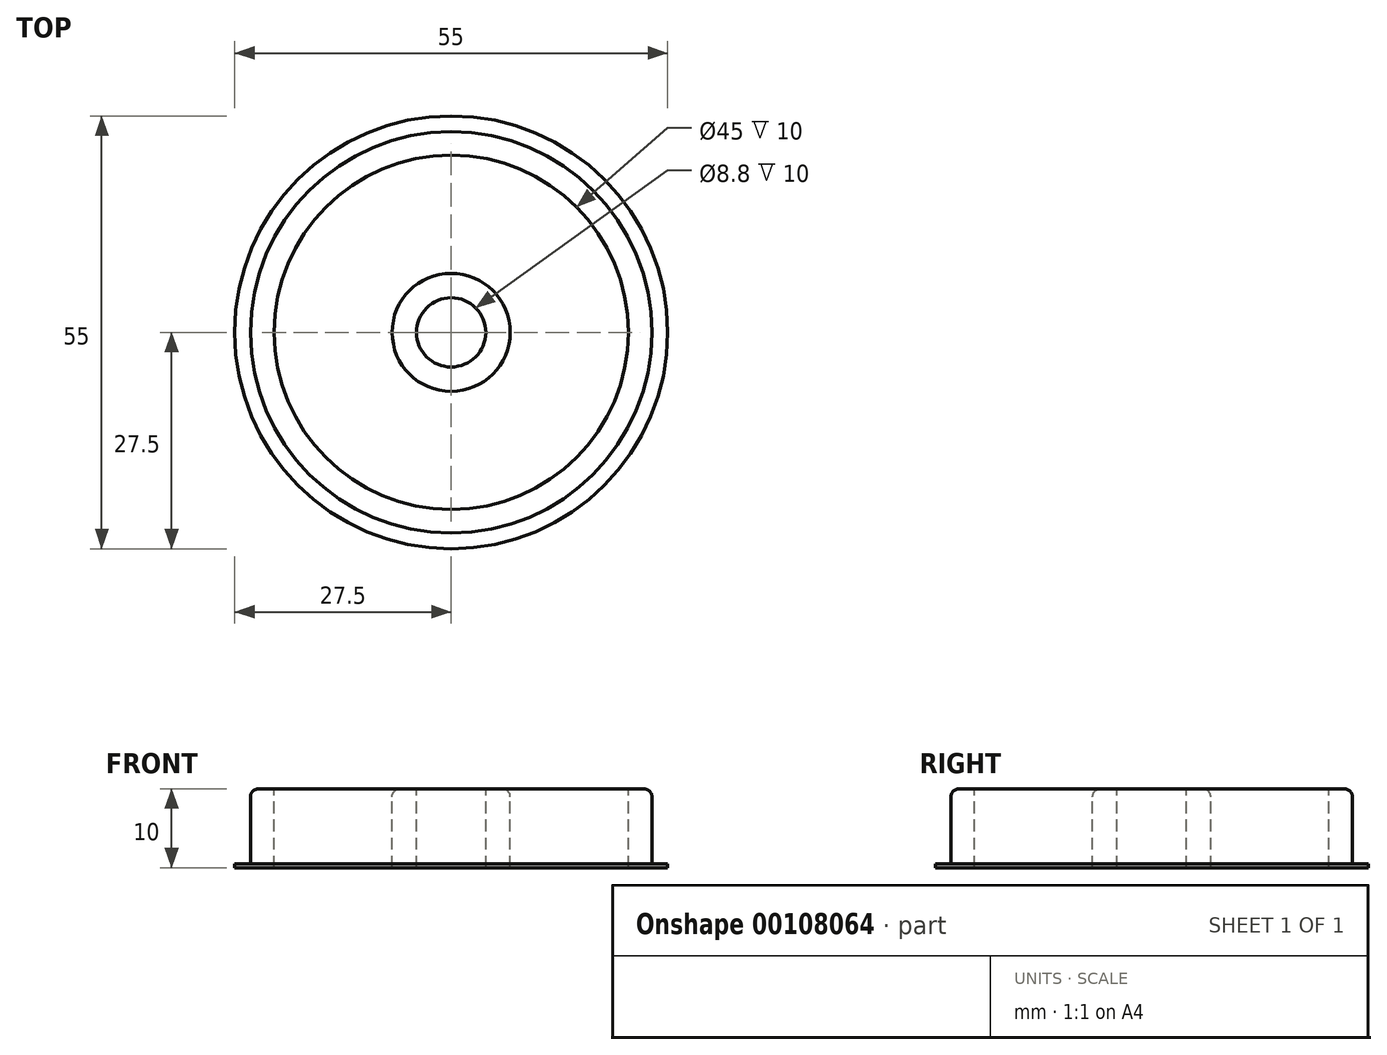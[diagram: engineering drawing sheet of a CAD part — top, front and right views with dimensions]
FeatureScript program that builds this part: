
annotation { "Feature Type Name" : "Feature", "Feature Type Description" : "" }
export const myFeature = defineFeature(function(context is Context, id is Id, definition is map)
    precondition{}
    {
        {
            var Q0;
            Q0=qCreatedBy(makeId("Top.planeOp"),FACE);
            var sketch = newSketch(context, id + "F0", { "sketchPlane" : qUnion([Q0])});
            skCircle(sketch, "E0", {"center": v(0, 0) * mm, "radius": 25.5 * mm});
            skCircle(sketch, "E1", {"center": v(0, 0) * mm, "radius": 27.5 * mm});
            skSolve(sketch);
        }
        {
            var Q0;
            Q0=makeQuery(id+"F0.imprint","IMPRINT",FACE,{"disambiguationData":[TD([[makeQuery(id+"F0.imprint","IMPRINT",EDGE,{"derivedFrom":sQuery(id+"F0.wireOp",EDGE,"E0")}),1.0]])]});
            extrude(context, id + "F1", {"entities" : qUnion([Q0]), "depth" : 10 * mm});
        }
        {
            var Q0;
            Q0=makeQuery(id+"F0.imprint","IMPRINT",FACE,{"disambiguationData":[TD([[makeQuery(id+"F0.imprint","IMPRINT",EDGE,{"derivedFrom":sQuery(id+"F0.wireOp",EDGE,"E0")}),-1.0]])]});
            extrude(context, id + "F2", {"entities" : qUnion([Q0]), "operationType" : NewBodyOperationType.ADD, "depth" : 0.5 * mm});
        }
        {
            var Q0;
            Q0=makeQuery(id+"F1.opExtrude","CAP_FACE",FACE,{"disambiguationData":[OSD([sQuery(id+"F0.wireOp",EDGE,"E0")])],"isStart":false});
            var sketch = newSketch(context, id + "F3", { "sketchPlane" : qUnion([Q0])});
            skCircle(sketch, "E2", {"center": v(0, 0) * mm, "radius": 22.5 * mm});
            skCircle(sketch, "E3", {"center": v(0, 0) * mm, "radius": 7.5 * mm});
            skSolve(sketch);
        }
        {
            var Q0;
            Q0=makeQuery(id+"F3.imprint","IMPRINT",FACE,{"disambiguationData":[TD([[makeQuery(id+"F3.imprint","IMPRINT",EDGE,{"derivedFrom":sQuery(id+"F3.wireOp",EDGE,"E2")}),1.0]])]});
            extrude(context, id + "F4", {"entities" : qUnion([Q0]), "operationType" : NewBodyOperationType.REMOVE, "endBound" : BoundingType.THROUGH_ALL, "oppositeDirection" : true, "depth" : 25 * mm});
        }
        {
            var Q0;
            Q0=makeQuery(id+"F1.opExtrude","CAP_FACE",FACE,{"disambiguationData":[OSD([sQuery(id+"F0.wireOp",EDGE,"E0")])],"isStart":false});
            var sketch = newSketch(context, id + "F5", { "sketchPlane" : qUnion([Q0])});
            skCircle(sketch, "E4", {"center": v(0, 0) * mm, "radius": 7.5 * mm, "construction": true});
            skCircle(sketch, "E5", {"center": v(0, 0) * mm, "radius": 22.5 * mm, "construction": true});
            skLineSegment(sketch, "E6", {"start": v(22.5, -2.5) * mm, "end": v(22.5, 2.5) * mm});
            skPoint(sketch, "E7", {"position": v(22.5, 0) * mm});
            skLineSegment(sketch, "E8", {"start": v(6.9, 2.5) * mm, "end": v(6.9, -2.5) * mm});
            skPoint(sketch, "E9", {"position": v(6.9, 0) * mm});
            skLineSegment(sketch, "E10", {"start": v(6.9, 2.5) * mm, "end": v(22.5, 2.5) * mm});
            skLineSegment(sketch, "E11", {"start": v(22.5, -2.5) * mm, "end": v(6.9, -2.5) * mm});
            skSolve(sketch);
        }
        {
            var Q0;
            {var subQ4=sQuery(id+"F5.wireOp",EDGE,"E10");var subQ5=makeQuery(id+"F4.boolean.opBoolean","COPY",EDGE,{"derivedFrom":makeQuery(id+"F4.opExtrude","CAP_EDGE",EDGE,{"disambiguationData":[OSD([sQuery(id+"F3.wireOp",EDGE,"E3")])],"isStart":true})});var subQ6=makeQuery(id+"F5.imprint","INTERSECT",VERTEX,{"derivedFrom":[subQ5,subQ4]});Q0=makeQuery(id+"F5.imprint","IMPRINT",FACE,{"disambiguationData":[TD([[makeQuery(id+"F5.imprint","IMPRINT",EDGE,{"disambiguationData":[TD([[subQ6,-1.0]])],"derivedFrom":subQ4}),-1.0]])]});}
            var Q1;
            {var subQ0=sQuery(id+"F0.wireOp",EDGE,"E0");Q1=makeQuery(id+"F4.boolean.opBoolean","SPLIT",FACE,{"disambiguationData":[TD([makeQuery(id+"F4.opExtrude","SWEPT_FACE",FACE,{"disambiguationData":[OSD([sQuery(id+"F3.wireOp",EDGE,"E3")])]})])],"derivedFrom":makeQuery(id+"F2.boolean.opBoolean","MERGE",FACE,{"derivedFrom":[makeQuery(id+"F1.opExtrude","CAP_FACE",FACE,{"disambiguationData":[OSD([subQ0])],"isStart":true}),makeQuery(id+"F2.opExtrude","CAP_FACE",FACE,{"disambiguationData":[OSD([subQ0,sQuery(id+"F0.wireOp",EDGE,"E1")])],"isStart":true})]})});}
            extrude(context, id + "F6", {"entities" : qUnion([Q0]), "operationType" : NewBodyOperationType.ADD, "endBound" : BoundingType.UP_TO_SURFACE, "oppositeDirection" : true, "endBoundEntityFace" : qUnion([Q1]), "depth" : 25 * mm});
        }
        {
            var Q0;
            {var subQ0=sQuery(id+"F5.wireOp",EDGE,"E11");var subQ1=sQuery(id+"F5.wireOp",EDGE,"E10");var subQ3=sQuery(id+"F3.wireOp",EDGE,"E2");var subQ5=makeQuery(id+"F5tnbVkuxQUPv66_1.1.F6.opExtrude","SWEPT_FACE",FACE,{"disambiguationData":[OSD([subQ1])]});Q0=makeQuery(id+"F5tnbVkuxQUPv66_1.2.F6.boolean.opBoolean","SPLIT",EDGE,{"disambiguationData":[TD([subQ5])],"derivedFrom":makeQuery(id+"F5tnbVkuxQUPv66_1.1.F6.boolean.opBoolean","SPLIT",EDGE,{"disambiguationData":[TD([makeQuery(id+"F6.opExtrude","SWEPT_FACE",FACE,{"disambiguationData":[OSD([subQ0])]})])],"derivedFrom":makeQuery(id+"F4.boolean.opBoolean","COPY",EDGE,{"derivedFrom":makeQuery(id+"F4.opExtrude","CAP_EDGE",EDGE,{"disambiguationData":[OSD([subQ3])],"isStart":true})})})});}
            var Q1;
            Q1=makeQuery(id+"F5tnbVkuxQUPv66_1.1.F6.opExtrude","CAP_EDGE",EDGE,{"disambiguationData":[OSD([sQuery(id+"F5.wireOp",EDGE,"E10")])],"isStart":true});
            var Q2;
            Q2=makeQuery(id+"F5tnbVkuxQUPv66_1.1.F6.opExtrude","CAP_EDGE",EDGE,{"disambiguationData":[OSD([sQuery(id+"F5.wireOp",EDGE,"E11")])],"isStart":true});
            var Q3;
            {var subQ1=sQuery(id+"F5.wireOp",EDGE,"E10");var subQ3=sQuery(id+"F3.wireOp",EDGE,"E2");Q3=makeQuery(id+"F5tnbVkuxQUPv66_1.1.F6.boolean.opBoolean","SPLIT",EDGE,{"disambiguationData":[TD([makeQuery(id+"F6.opExtrude","SWEPT_FACE",FACE,{"disambiguationData":[OSD([subQ1])]})])],"derivedFrom":makeQuery(id+"F4.boolean.opBoolean","COPY",EDGE,{"derivedFrom":makeQuery(id+"F4.opExtrude","CAP_EDGE",EDGE,{"disambiguationData":[OSD([subQ3])],"isStart":true})})});}
            var Q4;
            Q4=makeQuery(id+"F6.opExtrude","CAP_EDGE",EDGE,{"disambiguationData":[OSD([sQuery(id+"F5.wireOp",EDGE,"E10")])],"isStart":true});
            var Q5;
            {var subQ1=sQuery(id+"F5.wireOp",EDGE,"E10");var subQ2=sQuery(id+"F3.wireOp",EDGE,"E3");Q5=makeQuery(id+"F5tnbVkuxQUPv66_1.1.F6.boolean.opBoolean","SPLIT",EDGE,{"disambiguationData":[TD([makeQuery(id+"F6.opExtrude","SWEPT_FACE",FACE,{"disambiguationData":[OSD([subQ1])]})])],"derivedFrom":makeQuery(id+"F4.boolean.opBoolean","COPY",EDGE,{"derivedFrom":makeQuery(id+"F4.opExtrude","CAP_EDGE",EDGE,{"disambiguationData":[OSD([subQ2])],"isStart":true})})});}
            var Q6;
            {var subQ0=sQuery(id+"F5.wireOp",EDGE,"E10");var subQ1=makeQuery(id+"F5tnbVkuxQUPv66_1.1.F6.opExtrude","SWEPT_FACE",FACE,{"disambiguationData":[OSD([subQ0])]});var subQ2=sQuery(id+"F5.wireOp",EDGE,"E11");var subQ3=sQuery(id+"F3.wireOp",EDGE,"E3");Q6=makeQuery(id+"F5tnbVkuxQUPv66_1.2.F6.boolean.opBoolean","SPLIT",EDGE,{"disambiguationData":[TD([subQ1])],"derivedFrom":makeQuery(id+"F5tnbVkuxQUPv66_1.1.F6.boolean.opBoolean","SPLIT",EDGE,{"disambiguationData":[TD([makeQuery(id+"F6.opExtrude","SWEPT_FACE",FACE,{"disambiguationData":[OSD([subQ2])]})])],"derivedFrom":makeQuery(id+"F4.boolean.opBoolean","COPY",EDGE,{"derivedFrom":makeQuery(id+"F4.opExtrude","CAP_EDGE",EDGE,{"disambiguationData":[OSD([subQ3])],"isStart":true})})})});}
            var Q7;
            Q7=makeQuery(id+"F5tnbVkuxQUPv66_1.2.F6.opExtrude","CAP_EDGE",EDGE,{"disambiguationData":[OSD([sQuery(id+"F5.wireOp",EDGE,"E11")])],"isStart":true});
            var Q8;
            Q8=makeQuery(id+"F5tnbVkuxQUPv66_1.2.F6.opExtrude","CAP_EDGE",EDGE,{"disambiguationData":[OSD([sQuery(id+"F5.wireOp",EDGE,"E10")])],"isStart":true});
            var Q9;
            {var subQ0=sQuery(id+"F5.wireOp",EDGE,"E11");var subQ1=sQuery(id+"F5.wireOp",EDGE,"E10");var subQ2=sQuery(id+"F3.wireOp",EDGE,"E3");var subQ8=makeQuery(id+"F5tnbVkuxQUPv66_1.2.F6.opExtrude","SWEPT_FACE",FACE,{"disambiguationData":[OSD([subQ1])]});var subQ10=makeQuery(id+"F6.opExtrude","SWEPT_FACE",FACE,{"disambiguationData":[OSD([subQ0])]});Q9=makeQuery(id+"F5tnbVkuxQUPv66_1.3.F6.boolean.opBoolean","SPLIT",EDGE,{"disambiguationData":[TD([subQ8])],"derivedFrom":makeQuery(id+"F5tnbVkuxQUPv66_1.2.F6.boolean.opBoolean","SPLIT",EDGE,{"disambiguationData":[TD([subQ10])],"derivedFrom":makeQuery(id+"F5tnbVkuxQUPv66_1.1.F6.boolean.opBoolean","SPLIT",EDGE,{"disambiguationData":[TD([subQ10])],"derivedFrom":makeQuery(id+"F4.boolean.opBoolean","COPY",EDGE,{"derivedFrom":makeQuery(id+"F4.opExtrude","CAP_EDGE",EDGE,{"disambiguationData":[OSD([subQ2])],"isStart":true})})})})});}
            var Q10;
            {var subQ0=sQuery(id+"F5.wireOp",EDGE,"E11");var subQ2=sQuery(id+"F3.wireOp",EDGE,"E3");var subQ5=makeQuery(id+"F6.opExtrude","SWEPT_FACE",FACE,{"disambiguationData":[OSD([subQ0])]});Q10=makeQuery(id+"F5tnbVkuxQUPv66_1.3.F6.boolean.opBoolean","SPLIT",EDGE,{"disambiguationData":[TD([subQ5])],"derivedFrom":makeQuery(id+"F5tnbVkuxQUPv66_1.2.F6.boolean.opBoolean","SPLIT",EDGE,{"disambiguationData":[TD([subQ5])],"derivedFrom":makeQuery(id+"F5tnbVkuxQUPv66_1.1.F6.boolean.opBoolean","SPLIT",EDGE,{"disambiguationData":[TD([subQ5])],"derivedFrom":makeQuery(id+"F4.boolean.opBoolean","COPY",EDGE,{"derivedFrom":makeQuery(id+"F4.opExtrude","CAP_EDGE",EDGE,{"disambiguationData":[OSD([subQ2])],"isStart":true})})})})});}
            var Q11;
            Q11=makeQuery(id+"F6.opExtrude","CAP_EDGE",EDGE,{"disambiguationData":[OSD([sQuery(id+"F5.wireOp",EDGE,"E11")])],"isStart":true});
            var Q12;
            Q12=makeQuery(id+"F5tnbVkuxQUPv66_1.3.F6.opExtrude","CAP_EDGE",EDGE,{"disambiguationData":[OSD([sQuery(id+"F5.wireOp",EDGE,"E10")])],"isStart":true});
            var Q13;
            Q13=makeQuery(id+"F5tnbVkuxQUPv66_1.3.F6.opExtrude","CAP_EDGE",EDGE,{"disambiguationData":[OSD([sQuery(id+"F5.wireOp",EDGE,"E11")])],"isStart":true});
            var Q14;
            {var subQ0=sQuery(id+"F5.wireOp",EDGE,"E11");var subQ1=sQuery(id+"F5.wireOp",EDGE,"E10");var subQ3=sQuery(id+"F3.wireOp",EDGE,"E2");var subQ8=makeQuery(id+"F5tnbVkuxQUPv66_1.2.F6.opExtrude","SWEPT_FACE",FACE,{"disambiguationData":[OSD([subQ1])]});var subQ10=makeQuery(id+"F6.opExtrude","SWEPT_FACE",FACE,{"disambiguationData":[OSD([subQ0])]});Q14=makeQuery(id+"F5tnbVkuxQUPv66_1.3.F6.boolean.opBoolean","SPLIT",EDGE,{"disambiguationData":[TD([subQ8])],"derivedFrom":makeQuery(id+"F5tnbVkuxQUPv66_1.2.F6.boolean.opBoolean","SPLIT",EDGE,{"disambiguationData":[TD([subQ10])],"derivedFrom":makeQuery(id+"F5tnbVkuxQUPv66_1.1.F6.boolean.opBoolean","SPLIT",EDGE,{"disambiguationData":[TD([subQ10])],"derivedFrom":makeQuery(id+"F4.boolean.opBoolean","COPY",EDGE,{"derivedFrom":makeQuery(id+"F4.opExtrude","CAP_EDGE",EDGE,{"disambiguationData":[OSD([subQ3])],"isStart":true})})})})});}
            var Q15;
            {var subQ0=sQuery(id+"F5.wireOp",EDGE,"E11");var subQ3=sQuery(id+"F3.wireOp",EDGE,"E2");var subQ7=makeQuery(id+"F6.opExtrude","SWEPT_FACE",FACE,{"disambiguationData":[OSD([subQ0])]});Q15=makeQuery(id+"F5tnbVkuxQUPv66_1.3.F6.boolean.opBoolean","SPLIT",EDGE,{"disambiguationData":[TD([subQ7])],"derivedFrom":makeQuery(id+"F5tnbVkuxQUPv66_1.2.F6.boolean.opBoolean","SPLIT",EDGE,{"disambiguationData":[TD([subQ7])],"derivedFrom":makeQuery(id+"F5tnbVkuxQUPv66_1.1.F6.boolean.opBoolean","SPLIT",EDGE,{"disambiguationData":[TD([subQ7])],"derivedFrom":makeQuery(id+"F4.boolean.opBoolean","COPY",EDGE,{"derivedFrom":makeQuery(id+"F4.opExtrude","CAP_EDGE",EDGE,{"disambiguationData":[OSD([subQ3])],"isStart":true})})})})});}
            var Q16;
            Q16=makeQuery(id+"F1.opExtrude","CAP_EDGE",EDGE,{"disambiguationData":[OSD([sQuery(id+"F0.wireOp",EDGE,"E0")])],"isStart":false});
            var Q17;
            Q17=makeQuery(id+"F5tnbVkuxQUPv66_1.1.F6.opExtrude","SWEPT_EDGE",EDGE,{"disambiguationData":[OSD([sQuery(id+"F3.wireOp",EDGE,"E2"),sQuery(id+"F5.wireOp",EDGE,"E10")])]});
            var Q18;
            Q18=makeQuery(id+"F5tnbVkuxQUPv66_1.1.F6.opExtrude","SWEPT_EDGE",EDGE,{"disambiguationData":[OSD([sQuery(id+"F3.wireOp",EDGE,"E2"),sQuery(id+"F5.wireOp",EDGE,"E11")])]});
            var Q19;
            Q19=makeQuery(id+"F6.opExtrude","SWEPT_EDGE",EDGE,{"disambiguationData":[OSD([sQuery(id+"F3.wireOp",EDGE,"E2"),sQuery(id+"F5.wireOp",EDGE,"E10")])]});
            var Q20;
            Q20=makeQuery(id+"F6.opExtrude","SWEPT_EDGE",EDGE,{"disambiguationData":[OSD([sQuery(id+"F3.wireOp",EDGE,"E3"),sQuery(id+"F5.wireOp",EDGE,"E10")])]});
            var Q21;
            Q21=makeQuery(id+"F5tnbVkuxQUPv66_1.1.F6.opExtrude","SWEPT_EDGE",EDGE,{"disambiguationData":[OSD([sQuery(id+"F3.wireOp",EDGE,"E3"),sQuery(id+"F5.wireOp",EDGE,"E11")])]});
            var Q22;
            Q22=makeQuery(id+"F5tnbVkuxQUPv66_1.1.F6.opExtrude","SWEPT_EDGE",EDGE,{"disambiguationData":[OSD([sQuery(id+"F3.wireOp",EDGE,"E3"),sQuery(id+"F5.wireOp",EDGE,"E10")])]});
            var Q23;
            Q23=makeQuery(id+"F5tnbVkuxQUPv66_1.2.F6.opExtrude","SWEPT_EDGE",EDGE,{"disambiguationData":[OSD([sQuery(id+"F3.wireOp",EDGE,"E3"),sQuery(id+"F5.wireOp",EDGE,"E11")])]});
            var Q24;
            Q24=makeQuery(id+"F5tnbVkuxQUPv66_1.2.F6.opExtrude","SWEPT_EDGE",EDGE,{"disambiguationData":[OSD([sQuery(id+"F3.wireOp",EDGE,"E2"),sQuery(id+"F5.wireOp",EDGE,"E11")])]});
            var Q25;
            Q25=makeQuery(id+"F5tnbVkuxQUPv66_1.2.F6.opExtrude","SWEPT_EDGE",EDGE,{"disambiguationData":[OSD([sQuery(id+"F3.wireOp",EDGE,"E2"),sQuery(id+"F5.wireOp",EDGE,"E10")])]});
            var Q26;
            Q26=makeQuery(id+"F5tnbVkuxQUPv66_1.2.F6.opExtrude","SWEPT_EDGE",EDGE,{"disambiguationData":[OSD([sQuery(id+"F3.wireOp",EDGE,"E3"),sQuery(id+"F5.wireOp",EDGE,"E10")])]});
            var Q27;
            Q27=makeQuery(id+"F5tnbVkuxQUPv66_1.3.F6.opExtrude","SWEPT_EDGE",EDGE,{"disambiguationData":[OSD([sQuery(id+"F3.wireOp",EDGE,"E3"),sQuery(id+"F5.wireOp",EDGE,"E11")])]});
            var Q28;
            Q28=makeQuery(id+"F5tnbVkuxQUPv66_1.3.F6.opExtrude","SWEPT_EDGE",EDGE,{"disambiguationData":[OSD([sQuery(id+"F3.wireOp",EDGE,"E2"),sQuery(id+"F5.wireOp",EDGE,"E11")])]});
            var Q29;
            Q29=makeQuery(id+"F6.opExtrude","SWEPT_EDGE",EDGE,{"disambiguationData":[OSD([sQuery(id+"F3.wireOp",EDGE,"E3"),sQuery(id+"F5.wireOp",EDGE,"E11")])]});
            var Q30;
            Q30=makeQuery(id+"F5tnbVkuxQUPv66_1.3.F6.opExtrude","SWEPT_EDGE",EDGE,{"disambiguationData":[OSD([sQuery(id+"F3.wireOp",EDGE,"E3"),sQuery(id+"F5.wireOp",EDGE,"E10")])]});
            var Q31;
            Q31=makeQuery(id+"F5tnbVkuxQUPv66_1.3.F6.opExtrude","SWEPT_EDGE",EDGE,{"disambiguationData":[OSD([sQuery(id+"F3.wireOp",EDGE,"E2"),sQuery(id+"F5.wireOp",EDGE,"E10")])]});
            var Q32;
            Q32=makeQuery(id+"F6.opExtrude","SWEPT_EDGE",EDGE,{"disambiguationData":[OSD([sQuery(id+"F3.wireOp",EDGE,"E2"),sQuery(id+"F5.wireOp",EDGE,"E11")])]});
            fillet(context, id + "F7", {"entities" : qUnion([Q0, Q1, Q2, Q3, Q4, Q5, Q6, Q7, Q8, Q9, Q10, Q11, Q12, Q13, Q14, Q15, Q16, Q17, Q18, Q19, Q20, Q21, Q22, Q23, Q24, Q25, Q26, Q27, Q28, Q29, Q30, Q31, Q32]), "radius" : 1 * mm, "tangentPropagation" : true, "allowEdgeOverflow" : false});
        }
        {
            var Q0;
            {var subQ0=sQuery(id+"F5.wireOp",EDGE,"E11");var subQ1=sQuery(id+"F5.wireOp",EDGE,"E10");var subQ2=sQuery(id+"F3.wireOp",EDGE,"E3");var subQ3=sQuery(id+"F3.wireOp",EDGE,"E2");var subQ4=sQuery(id+"F0.wireOp",EDGE,"E0");var subQ5=makeQuery(id+"F1.opExtrude","CAP_FACE",FACE,{"disambiguationData":[OSD([subQ4])],"isStart":false});Q0=makeQuery(id+"F5tnbVkuxQUPv66_1.3.F6.boolean.opBoolean","MERGE",FACE,{"derivedFrom":[makeQuery(id+"F5tnbVkuxQUPv66_1.2.F6.boolean.opBoolean","MERGE",FACE,{"derivedFrom":[makeQuery(id+"F5tnbVkuxQUPv66_1.1.F6.boolean.opBoolean","MERGE",FACE,{"derivedFrom":[makeQuery(id+"F6.boolean.opBoolean","MERGE",FACE,{"derivedFrom":[makeQuery(id+"F4.boolean.opBoolean","SPLIT",FACE,{"disambiguationData":[TD([makeQuery(id+"F1.opExtrude","SWEPT_FACE",FACE,{"disambiguationData":[OSD([subQ4])]})])],"derivedFrom":subQ5}),makeQuery(id+"F4.boolean.opBoolean","SPLIT",FACE,{"disambiguationData":[TD([makeQuery(id+"F4.opExtrude","SWEPT_FACE",FACE,{"disambiguationData":[OSD([subQ2])]})])],"derivedFrom":subQ5}),makeQuery(id+"F6.opExtrude","CAP_FACE",FACE,{"disambiguationData":[OSD([subQ3,subQ2,subQ1,subQ0])],"isStart":true})]}),makeQuery(id+"F5tnbVkuxQUPv66_1.1.F6.opExtrude","CAP_FACE",FACE,{"disambiguationData":[OSD([subQ3,subQ2,subQ1,subQ0])],"isStart":true})]}),makeQuery(id+"F5tnbVkuxQUPv66_1.2.F6.opExtrude","CAP_FACE",FACE,{"disambiguationData":[OSD([subQ3,subQ2,subQ1,subQ0])],"isStart":true})]}),makeQuery(id+"F5tnbVkuxQUPv66_1.3.F6.opExtrude","CAP_FACE",FACE,{"disambiguationData":[OSD([subQ3,subQ2,subQ1,subQ0])],"isStart":true})]});}
            var sketch = newSketch(context, id + "F8", { "sketchPlane" : qUnion([Q0])});
            skPoint(sketch, "E12", {"position": v(0, 0) * mm});
            skCircle(sketch, "E13", {"center": v(0, 0) * mm, "radius": 4.4 * mm});
            skSolve(sketch);
        }
        {
            var Q0;
            Q0=makeQuery(id+"F8.imprint","IMPRINT",FACE,{"disambiguationData":[TD([[makeQuery(id+"F8.imprint","IMPRINT",EDGE,{"derivedFrom":sQuery(id+"F8.wireOp",EDGE,"E13")}),1.0]])]});
            extrude(context, id + "F9", {"entities" : qUnion([Q0]), "operationType" : NewBodyOperationType.REMOVE, "endBound" : BoundingType.THROUGH_ALL, "oppositeDirection" : true, "depth" : 25 * mm});
        }
    });
